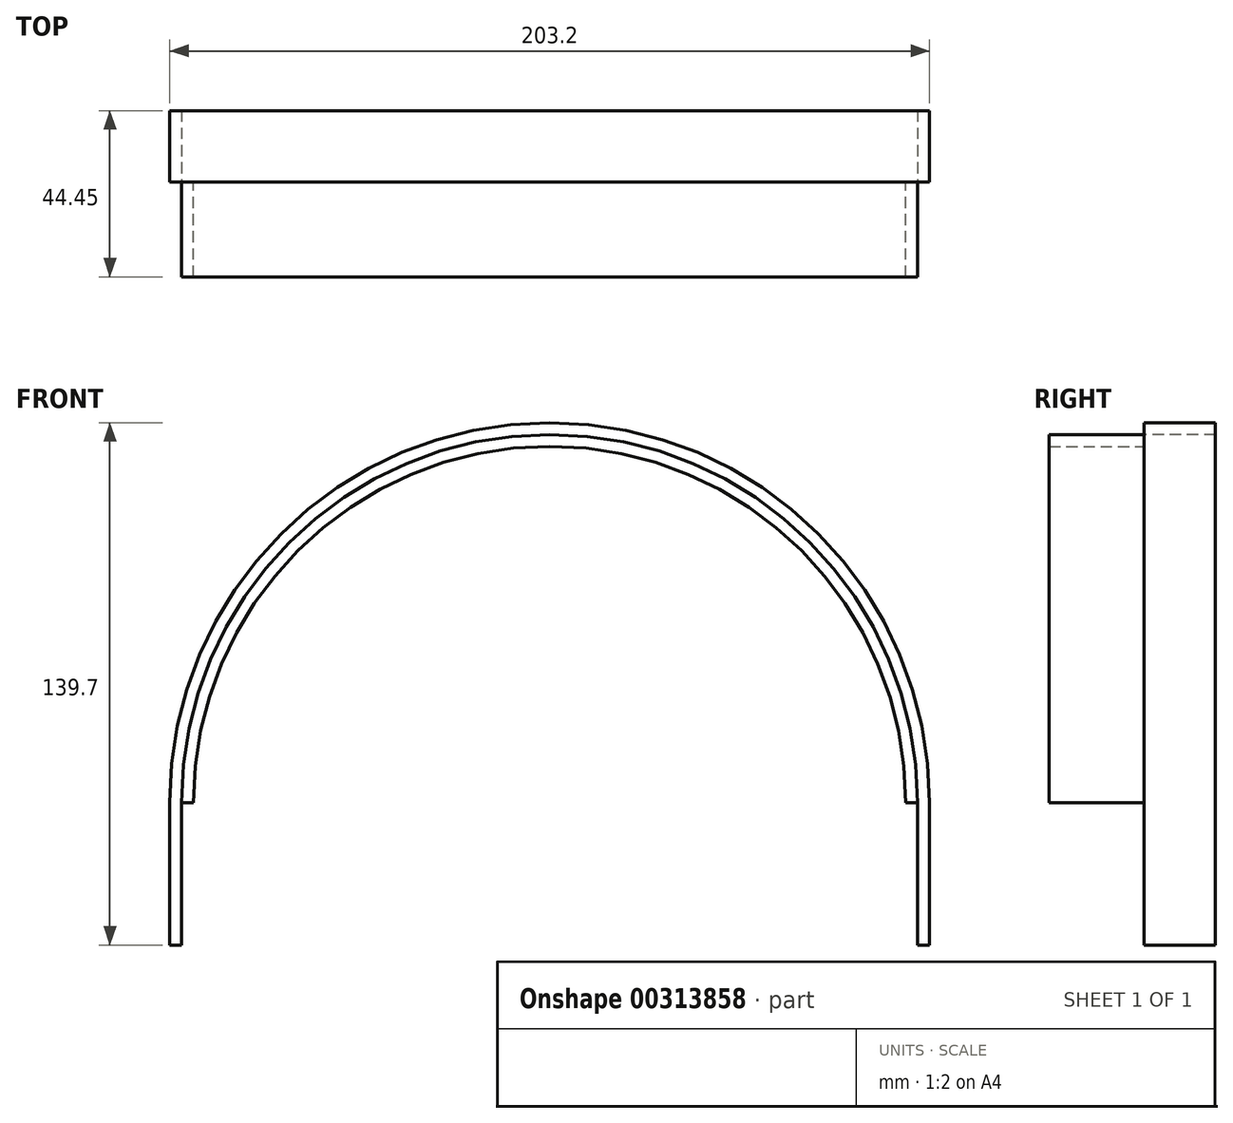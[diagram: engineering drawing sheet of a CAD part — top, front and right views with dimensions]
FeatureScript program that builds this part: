
annotation { "Feature Type Name" : "Feature", "Feature Type Description" : "" }
export const myFeature = defineFeature(function(context is Context, id is Id, definition is map)
    precondition{}
    {
        {
            var Q0;
            Q0=qCreatedBy(makeId("Front.planeOp"),FACE);
            var sketch = newSketch(context, id + "F0", { "sketchPlane" : qUnion([Q0])});
            skCircle(sketch, "E0", {"center": v(0, 0) * mm, "radius": 101.6 * mm});
            skLineSegment(sketch, "E1", {"start": v(-101.6, 0) * mm, "end": v(101.6, 0) * mm});
            skSolve(sketch);
        }
        {
            var Q0;
            {var subQ0=sQuery(id+"F0.wireOp",EDGE,"E1");Q0=makeQuery(id+"F0.imprint","IMPRINT",FACE,{"disambiguationData":[TD([[makeQuery(id+"F0.imprint","IMPRINT",EDGE,{"derivedFrom":subQ0}),1.0]])]});}
            extrude(context, id + "F1", {"entities" : qUnion([Q0]), "depth" : 19.05 * mm});
        }
        {
            var Q0;
            Q0=makeQuery(id+"F1.opExtrude","CAP_FACE",FACE,{"disambiguationData":[OSD([sQuery(id+"F0.wireOp",EDGE,"E0"),sQuery(id+"F0.wireOp",EDGE,"E1")])],"isStart":false});
            var sketch = newSketch(context, id + "F2", { "sketchPlane" : qUnion([Q0])});
            skArc(sketch, "E2", {"start": v(95.25, 0) * mm, "mid": v(0, 95.25) * mm, "end": v(-95.25, 0) * mm});
            skSolve(sketch);
        }
        {
            var Q0;
            {var subQ0=sQuery(id+"F2.wireOp",EDGE,"E2");Q0=makeQuery(id+"F2.imprint","IMPRINT",FACE,{"disambiguationData":[TD([[makeQuery(id+"F2.imprint","IMPRINT",EDGE,{"derivedFrom":subQ0}),1.0]])]});}
            extrude(context, id + "F3", {"entities" : qUnion([Q0]), "operationType" : NewBodyOperationType.REMOVE, "oppositeDirection" : true, "depth" : 25.4 * mm});
        }
        {
            var Q0;
            Q0=makeQuery(id+"F1.opExtrude","CAP_FACE",FACE,{"disambiguationData":[OSD([sQuery(id+"F0.wireOp",EDGE,"E0"),sQuery(id+"F0.wireOp",EDGE,"E1")])],"isStart":false});
            var sketch = newSketch(context, id + "F4", { "sketchPlane" : qUnion([Q0])});
            skArc(sketch, "E3", {"start": v(98.42, 0) * mm, "mid": v(0, 98.42) * mm, "end": v(-98.42, 0) * mm});
            skSolve(sketch);
        }
        {
            var Q0;
            {var subQ0=sQuery(id+"F4.wireOp",EDGE,"E3");Q0=makeQuery(id+"F4.imprint","IMPRINT",FACE,{"disambiguationData":[TD([[makeQuery(id+"F4.imprint","IMPRINT",EDGE,{"derivedFrom":subQ0}),1.0]])]});}
            extrude(context, id + "F5", {"entities" : qUnion([Q0]), "operationType" : NewBodyOperationType.REMOVE, "oppositeDirection" : true, "depth" : 25.4 * mm});
        }
        {
            var Q0;
            Q0=makeQuery(id+"F3.boolean.opBoolean","SPLIT",FACE,{"disambiguationData":[OD(0.0)],"derivedFrom":makeQuery(id+"F1.opExtrude","SWEPT_FACE",FACE,{"disambiguationData":[OSD([sQuery(id+"F0.wireOp",EDGE,"E1")])]})});
            var sketch = newSketch(context, id + "F6", { "sketchPlane" : qUnion([Q0])});
            skLineSegment(sketch, "E4.bottom", {"start": v(-101.6, 19.05) * mm, "end": v(-98.42, 19.05) * mm});
            skLineSegment(sketch, "E4.top", {"start": v(-101.6, 0) * mm, "end": v(-98.42, 0) * mm});
            skLineSegment(sketch, "E4.left", {"start": v(-101.6, 19.05) * mm, "end": v(-101.6, 0) * mm});
            skLineSegment(sketch, "E4.right", {"start": v(-98.42, 19.05) * mm, "end": v(-98.42, 0) * mm});
            skSolve(sketch);
        }
        {
            var Q0;
            Q0 = qSketchRegion(id + "F6", true);
            extrude(context, id + "F7", {"entities" : qUnion([Q0]), "operationType" : NewBodyOperationType.ADD, "depth" : 38.1 * mm});
        }
        {
            var Q0;
            Q0=makeQuery(id+"F3.boolean.opBoolean","SPLIT",FACE,{"disambiguationData":[OD(1.0)],"derivedFrom":makeQuery(id+"F1.opExtrude","SWEPT_FACE",FACE,{"disambiguationData":[OSD([sQuery(id+"F0.wireOp",EDGE,"E1")])]})});
            var sketch = newSketch(context, id + "F8", { "sketchPlane" : qUnion([Q0])});
            skLineSegment(sketch, "E5.bottom", {"start": v(98.42, 19.05) * mm, "end": v(101.6, 19.05) * mm});
            skLineSegment(sketch, "E5.top", {"start": v(98.42, 0) * mm, "end": v(101.6, 0) * mm});
            skLineSegment(sketch, "E5.left", {"start": v(98.42, 19.05) * mm, "end": v(98.42, 0) * mm});
            skLineSegment(sketch, "E5.right", {"start": v(101.6, 19.05) * mm, "end": v(101.6, 0) * mm});
            skSolve(sketch);
        }
        {
            var Q0;
            Q0 = qSketchRegion(id + "F8", true);
            extrude(context, id + "F9", {"entities" : qUnion([Q0]), "operationType" : NewBodyOperationType.ADD, "depth" : 38.1 * mm});
        }
        {
            var Q0;
            {var subQ0=sQuery(id+"F4.wireOp",EDGE,"E3");Q0=makeQuery(id+"F4.imprint","IMPRINT",FACE,{"disambiguationData":[TD([[makeQuery(id+"F4.imprint","IMPRINT",EDGE,{"derivedFrom":subQ0}),1.0]])]});}
            extrude(context, id + "F10", {"entities" : qUnion([Q0]), "operationType" : NewBodyOperationType.ADD, "depth" : 25.4 * mm});
        }
    });
